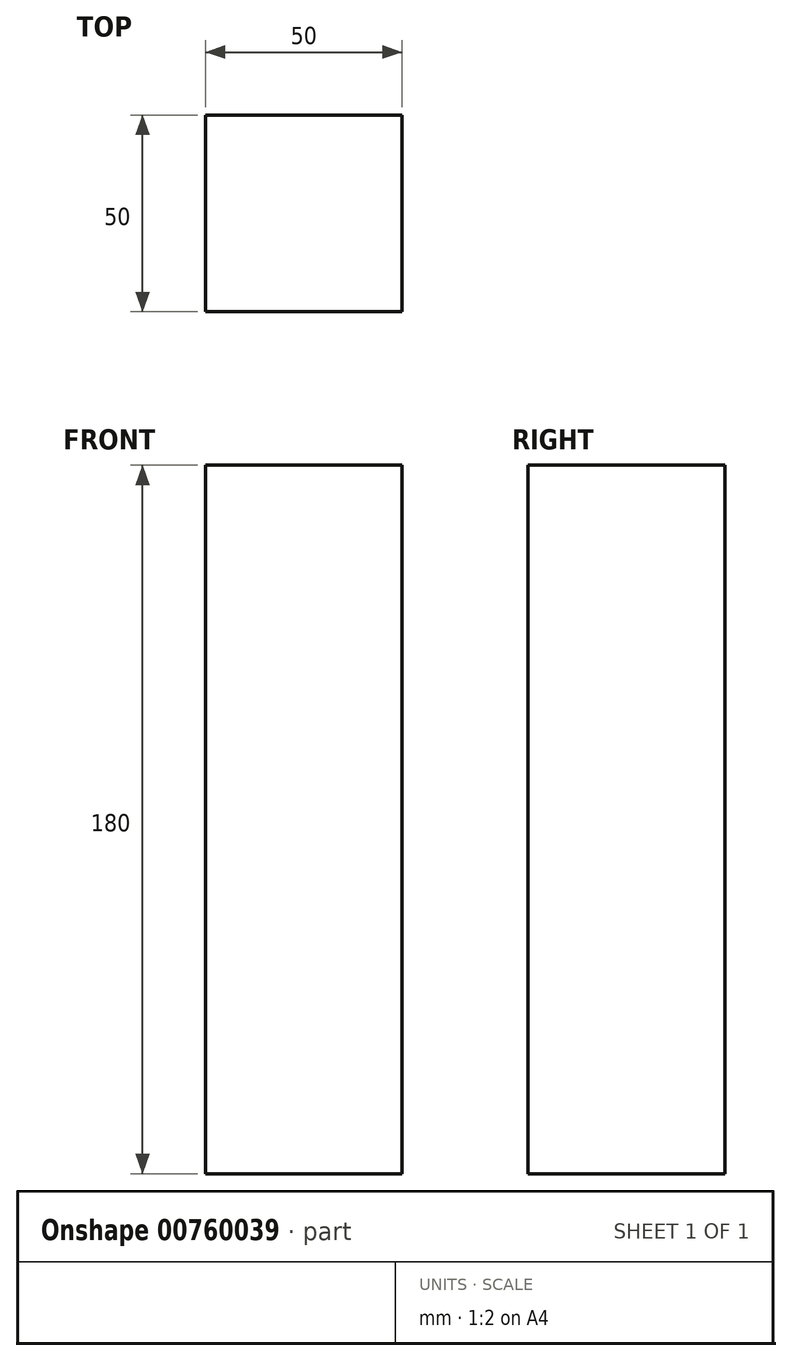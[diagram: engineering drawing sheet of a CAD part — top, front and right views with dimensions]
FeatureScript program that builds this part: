
annotation { "Feature Type Name" : "Feature", "Feature Type Description" : "" }
export const myFeature = defineFeature(function(context is Context, id is Id, definition is map)
    precondition{}
    {
        {
            var Q0;
            Q0=qCreatedBy(makeId("Top.planeOp"),FACE);
            var sketch = newSketch(context, id + "F0", { "sketchPlane" : qUnion([Q0])});
            skLineSegment(sketch, "E0.bottom", {"start": v(25, -25) * mm, "end": v(-25, -25) * mm});
            skLineSegment(sketch, "E0.top", {"start": v(25, 25) * mm, "end": v(-25, 25) * mm});
            skLineSegment(sketch, "E0.left", {"start": v(25, -25) * mm, "end": v(25, 25) * mm});
            skLineSegment(sketch, "E0.right", {"start": v(-25, -25) * mm, "end": v(-25, 25) * mm});
            skPoint(sketch, "E0.middle", {"position": v(0, 0) * mm});
            skSolve(sketch);
        }
        {
            var Q0;
            Q0=makeQuery(id+"F0.imprint","IMPRINT",FACE,{"disambiguationData":[TD([[makeQuery(id+"F0.imprint","IMPRINT",EDGE,{"derivedFrom":sQuery(id+"F0.wireOp",EDGE,"E0.bottom")}),-1.0]])]});
            extrude(context, id + "F1", {"entities" : qUnion([Q0]), "oppositeDirection" : true, "depth" : 180 * mm, "offsetDistance" : 25 * mm});
        }
    });
